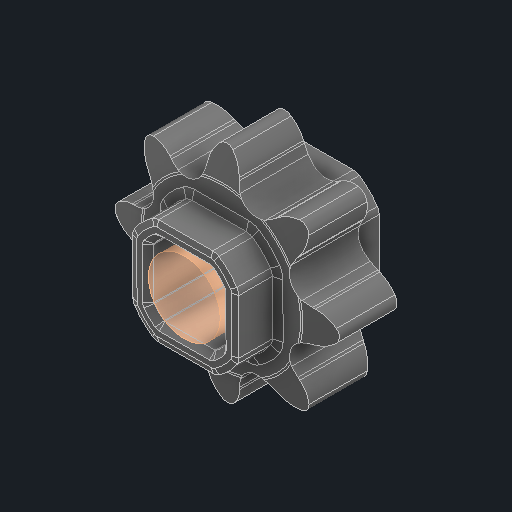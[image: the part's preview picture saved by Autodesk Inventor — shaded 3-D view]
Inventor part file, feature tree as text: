
AUTODESK INVENTOR PART (.ipt)
format: ipt  version: 2025 (Build 290162000, 162)  size: 688,128 bytes
history: native  units: in
note: dims shown in document units (in); Inventor stores cm internally (conversion verified against a paired STEP export)
features: other x5, sketch x1
ambient origin geometry x8: Origin, YZ Plane, XZ Plane, XY Plane, X Axis, Y Axis, Z Axis, Center Point
bodies: Solid1 (feature_tree)
feature tree (6):
  other  "6P 8T Sprocket.ipt"
  other  "Solid1::6P 8T Sprocket.ipt"
  other  "TaggingFeature1"
  sketch  "Sketch1"  dims[d0=0.3937in]
  other  "Srf1"
  other  "Srf1::Derived"
